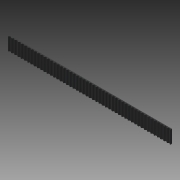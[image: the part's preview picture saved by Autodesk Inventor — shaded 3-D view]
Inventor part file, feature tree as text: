
AUTODESK INVENTOR PART (.ipt)
format: ipt  version: 2015 SP1 (Build 190203100, 203)  size: 441,856 bytes
history: native  units: mm
features: other x3, extrude x1, pattern_linear x1, sketch x1
ambient origin geometry x8: Origin, YZ Plane, XZ Plane, XY Plane, X Axis, Y Axis, Z Axis, Center Point
bodies: Solid1 (feature_tree)
feature tree (6):
  other  "Table"
  other  "T2.5 belt-01"
  other  "T2.5 belt-10"
  extrude  "Extrusion1"  Depth=0.2mm
  pattern_linear  "Rectangular Pattern1"  Spacing1=0.2mm  [1 undecoded]
  sketch  "Sketch1"  dims[d5=0.3mm d7=0.2mm d8=0.2mm d9=50.0mm d11=2.5mm d12=10.0mm d14=10.0mm d16=1.3mm d17=10.0mm d18=0.0mm d21=12.5mm]
note: 1 required parameter value undecoded (feature->parameter linkage not recoverable at this tier; creation-order binding heuristic only, values carry confidence <= 0.55)
